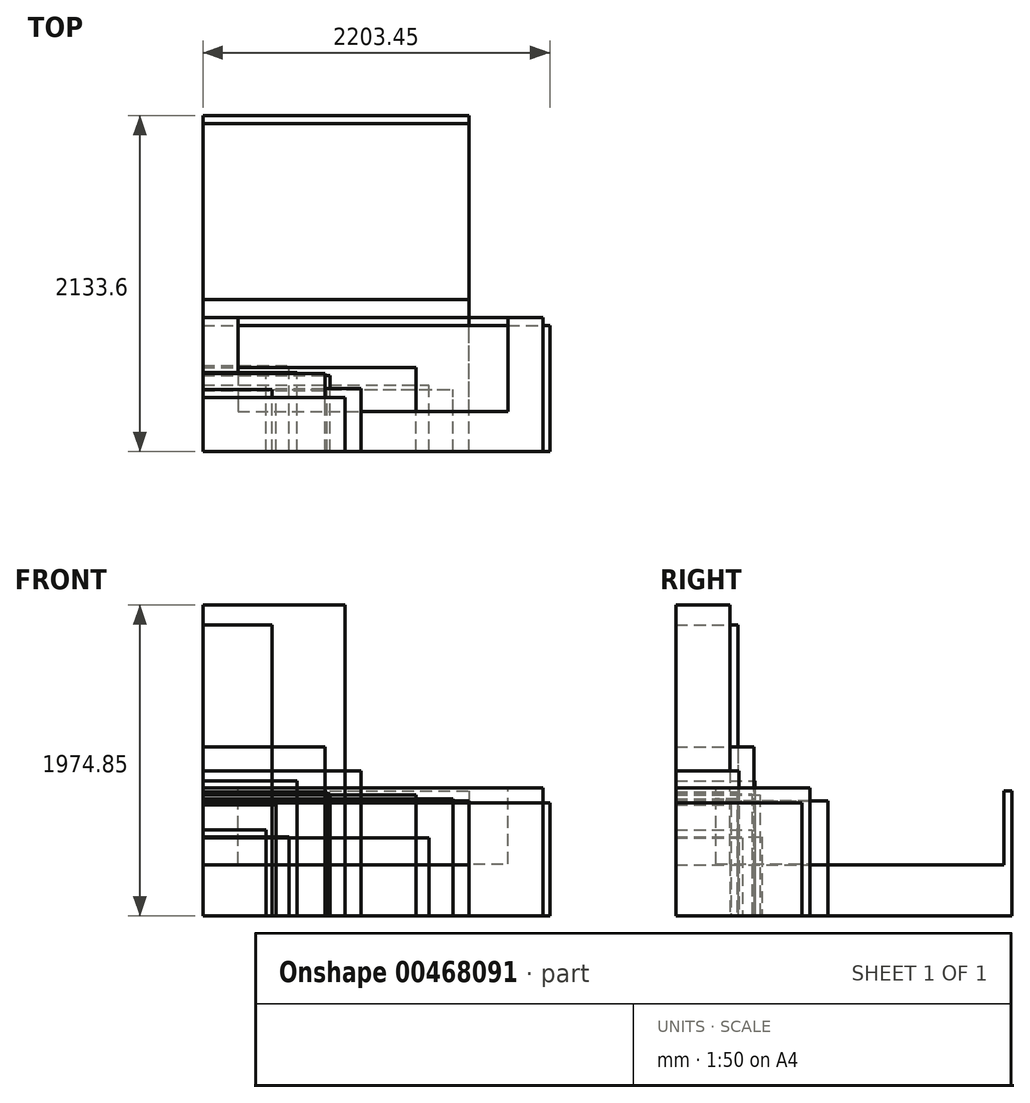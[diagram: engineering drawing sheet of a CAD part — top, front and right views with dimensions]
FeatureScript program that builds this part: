
annotation { "Feature Type Name" : "Feature", "Feature Type Description" : "" }
export const myFeature = defineFeature(function(context is Context, id is Id, definition is map)
    precondition{}
    {
        {
            var Q0;
            Q0=qCreatedBy(makeId("Top.planeOp"),FACE);
            var sketch = newSketch(context, id + "F0", { "sketchPlane" : qUnion([Q0])});
            skLineSegment(sketch, "E0.bottom", {"start": v(0, 0) * mm, "end": v(774.7, 0) * mm});
            skLineSegment(sketch, "E0.top", {"start": v(0, 495.3) * mm, "end": v(774.7, 495.3) * mm});
            skLineSegment(sketch, "E0.left", {"start": v(0, 0) * mm, "end": v(0, 495.3) * mm});
            skLineSegment(sketch, "E0.right", {"start": v(774.7, 0) * mm, "end": v(774.7, 495.3) * mm});
            skSolve(sketch);
        }
        {
            var Q0;
            Q0=makeQuery(id+"F0.imprint","IMPRINT",FACE,{"disambiguationData":[TD([[makeQuery(id+"F0.imprint","IMPRINT",EDGE,{"derivedFrom":sQuery(id+"F0.wireOp",EDGE,"E0.bottom")}),1.0]])]});
            extrude(context, id + "F1", {"entities" : qUnion([Q0]), "depth" : 1073.15 * mm});
        }
        {
            var Q0;
            Q0=qCreatedBy(makeId("Top.planeOp"),FACE);
            var sketch = newSketch(context, id + "F2", { "sketchPlane" : qUnion([Q0])});
            skLineSegment(sketch, "E1.bottom", {"start": v(0, 0) * mm, "end": v(901.7, 0) * mm});
            skLineSegment(sketch, "E1.top", {"start": v(0, 342.9) * mm, "end": v(901.7, 342.9) * mm});
            skLineSegment(sketch, "E1.left", {"start": v(0, 0) * mm, "end": v(0, 342.9) * mm});
            skLineSegment(sketch, "E1.right", {"start": v(901.7, 0) * mm, "end": v(901.7, 342.9) * mm});
            skSolve(sketch);
        }
        {
            var Q0;
            Q0=makeQuery(id+"F2.imprint","IMPRINT",FACE,{"disambiguationData":[TD([[makeQuery(id+"F2.imprint","IMPRINT",EDGE,{"derivedFrom":sQuery(id+"F2.wireOp",EDGE,"E1.bottom")}),1.0]])]});
            extrude(context, id + "F3", {"entities" : qUnion([Q0]), "depth" : 1974.85 * mm});
        }
        {
            var Q0;
            Q0=qCreatedBy(makeId("Top.planeOp"),FACE);
            var sketch = newSketch(context, id + "F4", { "sketchPlane" : qUnion([Q0])});
            skLineSegment(sketch, "E2.bottom", {"start": v(0, 0) * mm, "end": v(1689.1, 0) * mm});
            skLineSegment(sketch, "E2.top", {"start": v(0, 965.2) * mm, "end": v(1689.1, 965.2) * mm});
            skLineSegment(sketch, "E2.left", {"start": v(0, 0) * mm, "end": v(0, 965.2) * mm});
            skLineSegment(sketch, "E2.right", {"start": v(1689.1, 0) * mm, "end": v(1689.1, 965.2) * mm});
            skSolve(sketch);
        }
        {
            var Q0;
            Q0=makeQuery(id+"F4.imprint","IMPRINT",FACE,{"disambiguationData":[TD([[makeQuery(id+"F4.imprint","IMPRINT",EDGE,{"derivedFrom":sQuery(id+"F4.wireOp",EDGE,"E2.bottom")}),1.0]])]});
            extrude(context, id + "F5", {"entities" : qUnion([Q0]), "depth" : 730.25 * mm});
        }
        {
            var Q0;
            Q0=qCreatedBy(makeId("Top.planeOp"),FACE);
            var sketch = newSketch(context, id + "F6", { "sketchPlane" : qUnion([Q0])});
            skLineSegment(sketch, "E3.bottom", {"start": v(0, 0) * mm, "end": v(1587.5, 0) * mm});
            skLineSegment(sketch, "E3.top", {"start": v(0, 393.7) * mm, "end": v(1587.5, 393.7) * mm});
            skLineSegment(sketch, "E3.left", {"start": v(0, 0) * mm, "end": v(0, 393.7) * mm});
            skLineSegment(sketch, "E3.right", {"start": v(1587.5, 0) * mm, "end": v(1587.5, 393.7) * mm});
            skSolve(sketch);
        }
        {
            var Q0;
            Q0 = qSketchRegion(id + "F6", true);
            extrude(context, id + "F7", {"entities" : qUnion([Q0]), "depth" : 742.95 * mm});
        }
        {
            var Q0;
            Q0=qCreatedBy(makeId("Top.planeOp"),FACE);
            var sketch = newSketch(context, id + "F8", { "sketchPlane" : qUnion([Q0])});
            skLineSegment(sketch, "E4.bottom", {"start": v(0, 0) * mm, "end": v(2159, 0) * mm});
            skLineSegment(sketch, "E4.top", {"start": v(0, 850.9) * mm, "end": v(2159, 850.9) * mm});
            skLineSegment(sketch, "E4.left", {"start": v(0, 0) * mm, "end": v(0, 850.9) * mm});
            skLineSegment(sketch, "E4.right", {"start": v(2159, 0) * mm, "end": v(2159, 850.9) * mm});
            skSolve(sketch);
        }
        {
            var Q0;
            Q0 = qSketchRegion(id + "F8", true);
            extrude(context, id + "F9", {"entities" : qUnion([Q0]), "depth" : 812.8 * mm});
        }
        {
            var Q0;
            Q0=makeQuery(id+"F9.opExtrude","CAP_FACE",FACE,{"disambiguationData":[OSD([sQuery(id+"F8.wireOp",EDGE,"E4.bottom"),sQuery(id+"F8.wireOp",EDGE,"E4.top"),sQuery(id+"F8.wireOp",EDGE,"E4.left"),sQuery(id+"F8.wireOp",EDGE,"E4.right")])],"isStart":false});
            var sketch = newSketch(context, id + "F10", { "sketchPlane" : qUnion([Q0])});
            skLineSegment(sketch, "E5.bottom", {"start": v(222.25, 850.9) * mm, "end": v(1936.75, 850.9) * mm});
            skLineSegment(sketch, "E5.top", {"start": v(222.25, 254) * mm, "end": v(1936.75, 254) * mm});
            skLineSegment(sketch, "E5.left", {"start": v(222.25, 850.9) * mm, "end": v(222.25, 254) * mm});
            skLineSegment(sketch, "E5.right", {"start": v(1936.75, 850.9) * mm, "end": v(1936.75, 254) * mm});
            skSolve(sketch);
        }
        {
            var Q0;
            Q0=makeQuery(id+"F10.imprint","IMPRINT",FACE,{"disambiguationData":[TD([[makeQuery(id+"F10.imprint","IMPRINT",EDGE,{"derivedFrom":sQuery(id+"F10.wireOp",EDGE,"E5.bottom")}),-1.0]])]});
            extrude(context, id + "F11", {"entities" : qUnion([Q0]), "operationType" : NewBodyOperationType.REMOVE, "oppositeDirection" : true, "depth" : 482.6 * mm});
        }
        {
            var Q0;
            Q0=qCreatedBy(makeId("Top.planeOp"),FACE);
            var sketch = newSketch(context, id + "F12", { "sketchPlane" : qUnion([Q0])});
            skLineSegment(sketch, "E6.bottom", {"start": v(0, 0) * mm, "end": v(1435.1, 0) * mm});
            skLineSegment(sketch, "E6.top", {"start": v(0, 421.64) * mm, "end": v(1435.1, 421.64) * mm});
            skLineSegment(sketch, "E6.left", {"start": v(0, 0) * mm, "end": v(0, 421.64) * mm});
            skLineSegment(sketch, "E6.right", {"start": v(1435.1, 0) * mm, "end": v(1435.1, 421.64) * mm});
            skSolve(sketch);
        }
        {
            var Q0;
            Q0 = qSketchRegion(id + "F12", true);
            extrude(context, id + "F13", {"entities" : qUnion([Q0]), "depth" : 495.3 * mm});
        }
        {
            var Q0;
            Q0=qCreatedBy(makeId("Top.planeOp"),FACE);
            var sketch = newSketch(context, id + "F14", { "sketchPlane" : qUnion([Q0])});
            skLineSegment(sketch, "E7.bottom", {"start": v(0, 0) * mm, "end": v(1003.3, 0) * mm});
            skLineSegment(sketch, "E7.top", {"start": v(0, 400.05) * mm, "end": v(1003.3, 400.05) * mm});
            skLineSegment(sketch, "E7.left", {"start": v(0, 0) * mm, "end": v(0, 400.05) * mm});
            skLineSegment(sketch, "E7.right", {"start": v(1003.3, 0) * mm, "end": v(1003.3, 400.05) * mm});
            skSolve(sketch);
        }
        {
            var Q0;
            Q0 = qSketchRegion(id + "F14", true);
            extrude(context, id + "F15", {"entities" : qUnion([Q0]), "depth" : 920.75 * mm});
        }
        {
            var Q0;
            Q0=qCreatedBy(makeId("Top.planeOp"),FACE);
            var sketch = newSketch(context, id + "F16", { "sketchPlane" : qUnion([Q0])});
            skLineSegment(sketch, "E8.bottom", {"start": v(0, 0) * mm, "end": v(596.9, 0) * mm});
            skLineSegment(sketch, "E8.top", {"start": v(0, 501.65) * mm, "end": v(596.9, 501.65) * mm});
            skLineSegment(sketch, "E8.left", {"start": v(0, 0) * mm, "end": v(0, 501.65) * mm});
            skLineSegment(sketch, "E8.right", {"start": v(596.9, 0) * mm, "end": v(596.9, 501.65) * mm});
            skSolve(sketch);
        }
        {
            var Q0;
            Q0 = qSketchRegion(id + "F16", true);
            extrude(context, id + "F17", {"entities" : qUnion([Q0]), "depth" : 857.25 * mm});
        }
        {
            var Q0;
            Q0=qCreatedBy(makeId("Top.planeOp"),FACE);
            var sketch = newSketch(context, id + "F18", { "sketchPlane" : qUnion([Q0])});
            skLineSegment(sketch, "E9.bottom", {"start": v(0, 0) * mm, "end": v(438.15, 0) * mm});
            skLineSegment(sketch, "E9.top", {"start": v(0, 393.7) * mm, "end": v(438.15, 393.7) * mm});
            skLineSegment(sketch, "E9.left", {"start": v(0, 0) * mm, "end": v(0, 393.7) * mm});
            skLineSegment(sketch, "E9.right", {"start": v(438.15, 0) * mm, "end": v(438.15, 393.7) * mm});
            skSolve(sketch);
        }
        {
            var Q0;
            Q0 = qSketchRegion(id + "F18", true);
            extrude(context, id + "F19", {"entities" : qUnion([Q0]), "depth" : 1847.85 * mm});
        }
        {
            var Q0;
            Q0=qCreatedBy(makeId("Top.planeOp"),FACE);
            var sketch = newSketch(context, id + "F20", { "sketchPlane" : qUnion([Q0])});
            skLineSegment(sketch, "E10.bottom", {"start": v(0, 0) * mm, "end": v(1689.1, 0) * mm});
            skLineSegment(sketch, "E10.top", {"start": v(0, 2133.6) * mm, "end": v(1689.1, 2133.6) * mm});
            skLineSegment(sketch, "E10.left", {"start": v(0, 0) * mm, "end": v(0, 2133.6) * mm});
            skLineSegment(sketch, "E10.right", {"start": v(1689.1, 0) * mm, "end": v(1689.1, 2133.6) * mm});
            skSolve(sketch);
        }
        {
            var Q0;
            Q0 = qSketchRegion(id + "F20", true);
            extrude(context, id + "F21", {"entities" : qUnion([Q0]), "depth" : 323.85 * mm});
        }
        {
            var Q0;
            Q0=makeQuery(id+"F21.opExtrude","CAP_FACE",FACE,{"disambiguationData":[OSD([sQuery(id+"F20.wireOp",EDGE,"E10.bottom"),sQuery(id+"F20.wireOp",EDGE,"E10.top"),sQuery(id+"F20.wireOp",EDGE,"E10.left"),sQuery(id+"F20.wireOp",EDGE,"E10.right")])],"isStart":false});
            var sketch = newSketch(context, id + "F22", { "sketchPlane" : qUnion([Q0])});
            skLineSegment(sketch, "E11.bottom", {"start": v(0, 2133.6) * mm, "end": v(1689.1, 2133.6) * mm});
            skLineSegment(sketch, "E11.top", {"start": v(0, 2082.8) * mm, "end": v(1689.1, 2082.8) * mm});
            skLineSegment(sketch, "E11.left", {"start": v(0, 2133.6) * mm, "end": v(0, 2082.8) * mm});
            skLineSegment(sketch, "E11.right", {"start": v(1689.1, 2133.6) * mm, "end": v(1689.1, 2082.8) * mm});
            skSolve(sketch);
        }
        {
            var Q0;
            Q0=makeQuery(id+"F22.imprint","IMPRINT",FACE,{"disambiguationData":[TD([[makeQuery(id+"F22.imprint","IMPRINT",EDGE,{"derivedFrom":sQuery(id+"F22.wireOp",EDGE,"E11.bottom")}),-1.0]])]});
            extrude(context, id + "F23", {"entities" : qUnion([Q0]), "operationType" : NewBodyOperationType.ADD, "depth" : 469.9 * mm});
        }
        {
            var Q0;
            Q0=qCreatedBy(makeId("Top.planeOp"),FACE);
            var sketch = newSketch(context, id + "F24", { "sketchPlane" : qUnion([Q0])});
            skLineSegment(sketch, "E12.bottom", {"start": v(0, 0) * mm, "end": v(806.45, 0) * mm});
            skLineSegment(sketch, "E12.top", {"start": v(0, 482.6) * mm, "end": v(806.45, 482.6) * mm});
            skLineSegment(sketch, "E12.left", {"start": v(0, 0) * mm, "end": v(0, 482.6) * mm});
            skLineSegment(sketch, "E12.right", {"start": v(806.45, 0) * mm, "end": v(806.45, 482.6) * mm});
            skSolve(sketch);
        }
        {
            var Q0;
            Q0 = qSketchRegion(id + "F24", true);
            extrude(context, id + "F25", {"entities" : qUnion([Q0]), "depth" : 774.7 * mm});
        }
        {
            var Q0;
            Q0=qCreatedBy(makeId("Top.planeOp"),FACE);
            var sketch = newSketch(context, id + "F26", { "sketchPlane" : qUnion([Q0])});
            skLineSegment(sketch, "E13.bottom", {"start": v(0, 0) * mm, "end": v(400.05, 0) * mm});
            skLineSegment(sketch, "E13.top", {"start": v(0, 482.6) * mm, "end": v(400.05, 482.6) * mm});
            skLineSegment(sketch, "E13.left", {"start": v(0, 0) * mm, "end": v(0, 482.6) * mm});
            skLineSegment(sketch, "E13.right", {"start": v(400.05, 0) * mm, "end": v(400.05, 482.6) * mm});
            skSolve(sketch);
        }
        {
            var Q0;
            Q0 = qSketchRegion(id + "F26", true);
            extrude(context, id + "F27", {"entities" : qUnion([Q0]), "depth" : 546.1 * mm});
        }
        {
            var Q0;
            Q0=qCreatedBy(makeId("Top.planeOp"),FACE);
            var sketch = newSketch(context, id + "F28", { "sketchPlane" : qUnion([Q0])});
            skLineSegment(sketch, "E14.bottom", {"start": v(0, 0) * mm, "end": v(463.55, 0) * mm});
            skLineSegment(sketch, "E14.top", {"start": v(0, 349.25) * mm, "end": v(463.55, 349.25) * mm});
            skLineSegment(sketch, "E14.left", {"start": v(0, 0) * mm, "end": v(0, 349.25) * mm});
            skLineSegment(sketch, "E14.right", {"start": v(463.55, 0) * mm, "end": v(463.55, 349.25) * mm});
            skSolve(sketch);
        }
        {
            var Q0;
            Q0 = qSketchRegion(id + "F28", true);
            extrude(context, id + "F29", {"entities" : qUnion([Q0]), "depth" : 704.85 * mm});
        }
        {
            var Q0;
            Q0=qCreatedBy(makeId("Top.planeOp"),FACE);
            var sketch = newSketch(context, id + "F30", { "sketchPlane" : qUnion([Q0])});
            skLineSegment(sketch, "E15.bottom", {"start": v(0, 0) * mm, "end": v(1352.55, 0) * mm});
            skLineSegment(sketch, "E15.top", {"start": v(0, 533.4) * mm, "end": v(1352.55, 533.4) * mm});
            skLineSegment(sketch, "E15.left", {"start": v(0, 0) * mm, "end": v(0, 533.4) * mm});
            skLineSegment(sketch, "E15.right", {"start": v(1352.55, 0) * mm, "end": v(1352.55, 533.4) * mm});
            skSolve(sketch);
        }
        {
            var Q0;
            Q0 = qSketchRegion(id + "F30", true);
            extrude(context, id + "F31", {"entities" : qUnion([Q0]), "depth" : 768.35 * mm});
        }
        {
            var Q0;
            Q0=qCreatedBy(makeId("Top.planeOp"),FACE);
            var sketch = newSketch(context, id + "F32", { "sketchPlane" : qUnion([Q0])});
            skLineSegment(sketch, "E16.bottom", {"start": v(0, 0) * mm, "end": v(2203.45, 0) * mm});
            skLineSegment(sketch, "E16.top", {"start": v(0, 800.1) * mm, "end": v(2203.45, 800.1) * mm});
            skLineSegment(sketch, "E16.left", {"start": v(0, 0) * mm, "end": v(0, 800.1) * mm});
            skLineSegment(sketch, "E16.right", {"start": v(2203.45, 0) * mm, "end": v(2203.45, 800.1) * mm});
            skSolve(sketch);
        }
        {
            var Q0;
            Q0 = qSketchRegion(id + "F32", true);
            extrude(context, id + "F33", {"entities" : qUnion([Q0]), "depth" : 717.55 * mm});
        }
        {
            var Q0;
            Q0=qCreatedBy(makeId("Top.planeOp"),FACE);
            var sketch = newSketch(context, id + "F34", { "sketchPlane" : qUnion([Q0])});
            skLineSegment(sketch, "E17.bottom", {"start": v(0, 0) * mm, "end": v(787.4, 0) * mm});
            skLineSegment(sketch, "E17.top", {"start": v(0, 387.35) * mm, "end": v(787.4, 387.35) * mm});
            skLineSegment(sketch, "E17.left", {"start": v(0, 0) * mm, "end": v(0, 387.35) * mm});
            skLineSegment(sketch, "E17.right", {"start": v(787.4, 0) * mm, "end": v(787.4, 387.35) * mm});
            skSolve(sketch);
        }
        {
            var Q0;
            Q0 = qSketchRegion(id + "F34", true);
            extrude(context, id + "F35", {"entities" : qUnion([Q0]), "depth" : 787.4 * mm});
        }
        {
            var Q0;
            Q0=qCreatedBy(makeId("Top.planeOp"),FACE);
            var sketch = newSketch(context, id + "F36", { "sketchPlane" : qUnion([Q0])});
            skLineSegment(sketch, "E18.bottom", {"start": v(0, 0) * mm, "end": v(546.1, 0) * mm});
            skLineSegment(sketch, "E18.top", {"start": v(0, 546.1) * mm, "end": v(546.1, 546.1) * mm});
            skLineSegment(sketch, "E18.left", {"start": v(0, 0) * mm, "end": v(0, 546.1) * mm});
            skLineSegment(sketch, "E18.right", {"start": v(546.1, 0) * mm, "end": v(546.1, 546.1) * mm});
            skSolve(sketch);
        }
        {
            var Q0;
            Q0=makeQuery(id+"F36.imprint","IMPRINT",FACE,{"disambiguationData":[TD([[makeQuery(id+"F36.imprint","IMPRINT",EDGE,{"derivedFrom":sQuery(id+"F36.wireOp",EDGE,"E18.bottom")}),1.0]])]});
            extrude(context, id + "F37", {"entities" : qUnion([Q0]), "depth" : 501.65 * mm});
        }
    });
